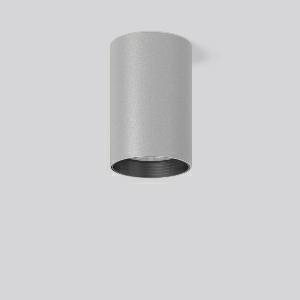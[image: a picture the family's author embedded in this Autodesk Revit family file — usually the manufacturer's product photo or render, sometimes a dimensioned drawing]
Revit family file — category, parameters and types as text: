
# Revit family: heledon_maxi_a_931228_004_1_a4da
name_source: partatom
category: Lighting Fixtures
units: mm (PartAtom-declared; Revit-internal decimal feet)

## family parameters
Cut with Voids When Loaded = No
Host = Face
Light Source = No
Part Type = Normal
Room Calculation Point = No
Round Connector Dimension = Use Diameter
Shared = No

## types (1)
- HELEDON maxi A (1 x LED Modul 940, 3750 lm, 4000)
    Apparent Load = 35 VA
    Approval mark = CE
    CIE Flux Codes = 96 100 100 100 100
    Color Rendering = 92
    Color Temperature = 4000
    Default Elevation = 1800 mm
    Description = Series: HELEDON maxi
Cylindrical surface-mounted downlight. Housing: die-cast aluminium, powder-coated. Internal ceiling frame polycarbonate with bayonet mounting. Black plastic ring and recessed LED to prevent glare from the side. Optical assembly with lens made of plastic (polycarbonate) for the best homogeneous light distribution - can be changed without tools. Best colour rendering index Ra>90. Suitable for Ceiling mounting. Easy installation with a separate ceiling frame with bayonet mounting and plug connection. Driver integrated. Connected via plug-in connector. High quality converter without flickering and stroboscopic effect. The following accessories can be mounted without use of tools: interchangeable lenses, decorative glasses, honeycomb louvre, clear and frosted diffusers, white interchangeable plastic ring. 
Colour: silver
Diameter: 123 mm
Height: 183 mm
Lamp: LED
Socket: without socket
Colour temperature: 4000K
Colour rendering index (CRI): 92
System power: 35 W
Rated luminous flux: 3750 lm
Luminous efficiency: 107 lm/W
Control gear: Regulated power supply
Protection class: I
Type of protection: IP 20
    Height = 183 mm
    Lamp = 1 x LED Modul 940
    Lamp Light Flux = 3750 lm
    Lamp count = 1
    Length = 123 mm
    Lifetime = 50000 h
    Luminous efficacy = 107 lm/W
    Manufacturer = RZB
    ModVariant = No
    Model = 931228.004.1
    Mounting Place = Ceiling
    Mounting Type = Surface mounted
    Number of Poles = 1
    OnlyDefault = Yes
    Power Factor = 1
    Product Name = HELEDON maxi A
    Product group = Surface mounted downlights
    ProductGroupID = 302
    Protection Class = Protection class I
    Protection Degree = IP 20
    RLX_Detail_Level = 1
    RLX_Emergency_Light_Flux = 0 lm
    RLX_Emergency_Type = 0
    RLX_Emergency_Type_DB = No
    RlxData = <blob elided: 99821 chars, md5=f211402d>
    Socket = socket
    Standby Power = 0 W
    System Light Flux = 3750 lm
    System Power = 35 W
    Type Comments = Product without accessories
    Type Image = 931193.004.jpg
    URL = http://relux.com
    VarID = ---
    Voltage = 230 V
    Voltage Range = 220-240 V
    Weight = 0.00 kg
    Width = 0 mm  [stored 0 ft]

note: [stored X ft] marks values corroborated as IEEE doubles in the binary element streams (Revit-internal decimal feet)

## geometry (parser evidence)
native form markers: Blend x4, Sweep x10
no freeform markers — native parametric forms only
